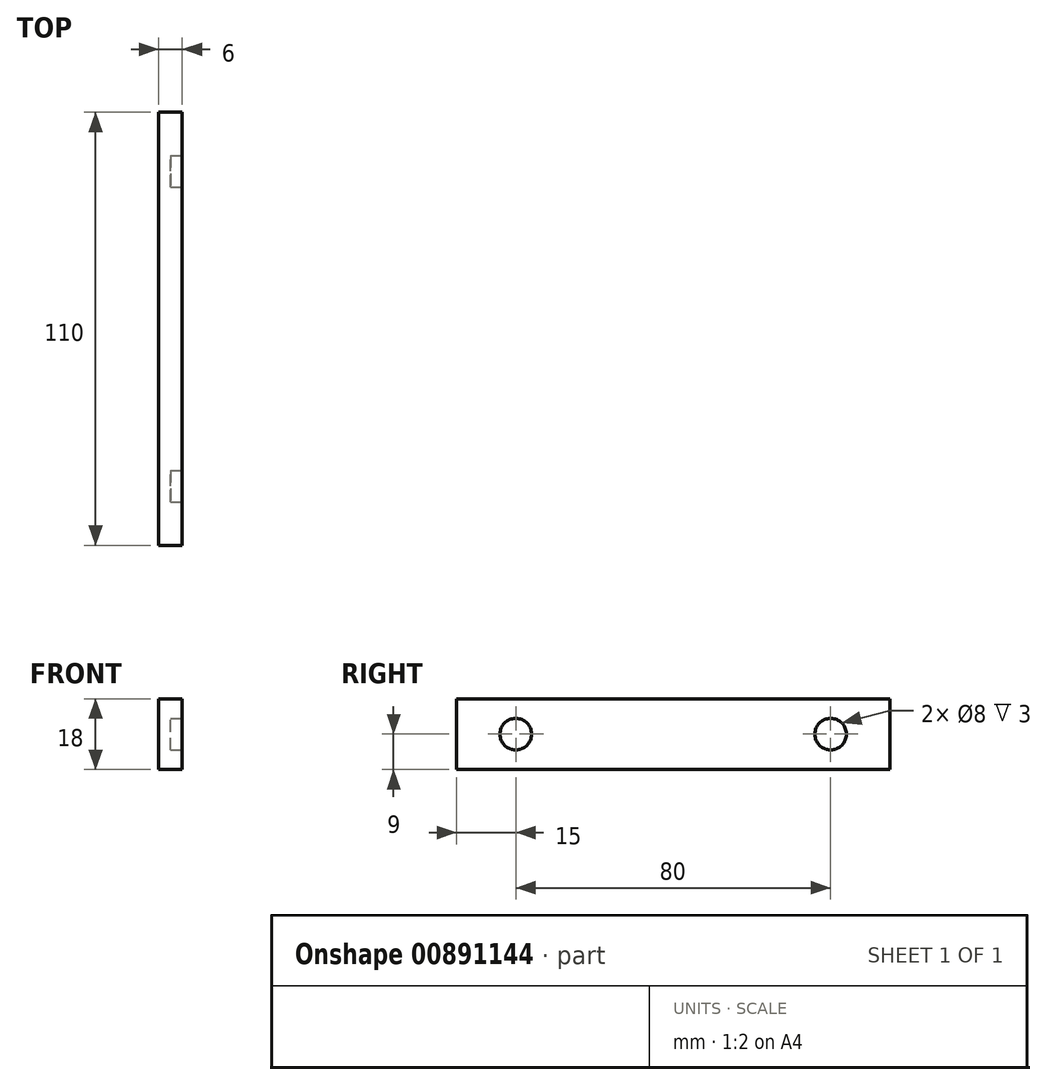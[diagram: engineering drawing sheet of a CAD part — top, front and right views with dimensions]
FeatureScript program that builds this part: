
annotation { "Feature Type Name" : "Feature", "Feature Type Description" : "" }
export const myFeature = defineFeature(function(context is Context, id is Id, definition is map)
    precondition{}
    {
        {
            var Q0;
            Q0=qCreatedBy(makeId("Right.planeOp"),FACE);
            var sketch = newSketch(context, id + "F0", { "sketchPlane" : qUnion([Q0])});
            skLineSegment(sketch, "E0.bottom", {"start": v(-55, -9) * mm, "end": v(55, -9) * mm});
            skLineSegment(sketch, "E0.top", {"start": v(-55, 9) * mm, "end": v(55, 9) * mm});
            skLineSegment(sketch, "E0.left", {"start": v(-55, -9) * mm, "end": v(-55, 9) * mm});
            skLineSegment(sketch, "E0.right", {"start": v(55, -9) * mm, "end": v(55, 9) * mm});
            skPoint(sketch, "E0.middle", {"position": v(0, 0) * mm});
            skLineSegment(sketch, "E1", {"start": v(0, 0) * mm, "end": v(0, 59.43) * mm, "construction": true});
            skSolve(sketch);
        }
        {
            var Q0;
            Q0 = qSketchRegion(id + "F0", true);
            extrude(context, id + "F1", {"entities" : qUnion([Q0]), "endBound" : BoundingType.SYMMETRIC, "depth" : 6 * mm, "offsetDistance" : 25 * mm});
        }
        {
            var Q0;
            Q0=makeQuery(id+"F1.opExtrude","CAP_FACE",FACE,{"disambiguationData":[OSD([sQuery(id+"F0.wireOp",EDGE,"E0.bottom"),sQuery(id+"F0.wireOp",EDGE,"E0.top"),sQuery(id+"F0.wireOp",EDGE,"E0.left"),sQuery(id+"F0.wireOp",EDGE,"E0.right")])],"isStart":false});
            var sketch = newSketch(context, id + "F2", { "sketchPlane" : qUnion([Q0])});
            skCircle(sketch, "E2", {"center": v(-40, 0) * mm, "radius": 4 * mm});
            skLineSegment(sketch, "E3", {"start": v(0, 0) * mm, "end": v(0, 23.32) * mm, "construction": true});
            skPoint(sketch, "E3.endSnap0", {"position": v(0, 9) * mm});
            skCircle(sketch, "E4.MirrorC", {"center": v(40, 0) * mm, "radius": 4 * mm});
            skSolve(sketch);
        }
        {
            var Q0;
            Q0 = qSketchRegion(id + "F2", true);
            extrude(context, id + "F3", {"entities" : qUnion([Q0]), "operationType" : NewBodyOperationType.REMOVE, "oppositeDirection" : true, "depth" : 3 * mm, "offsetDistance" : 25 * mm});
        }
    });
